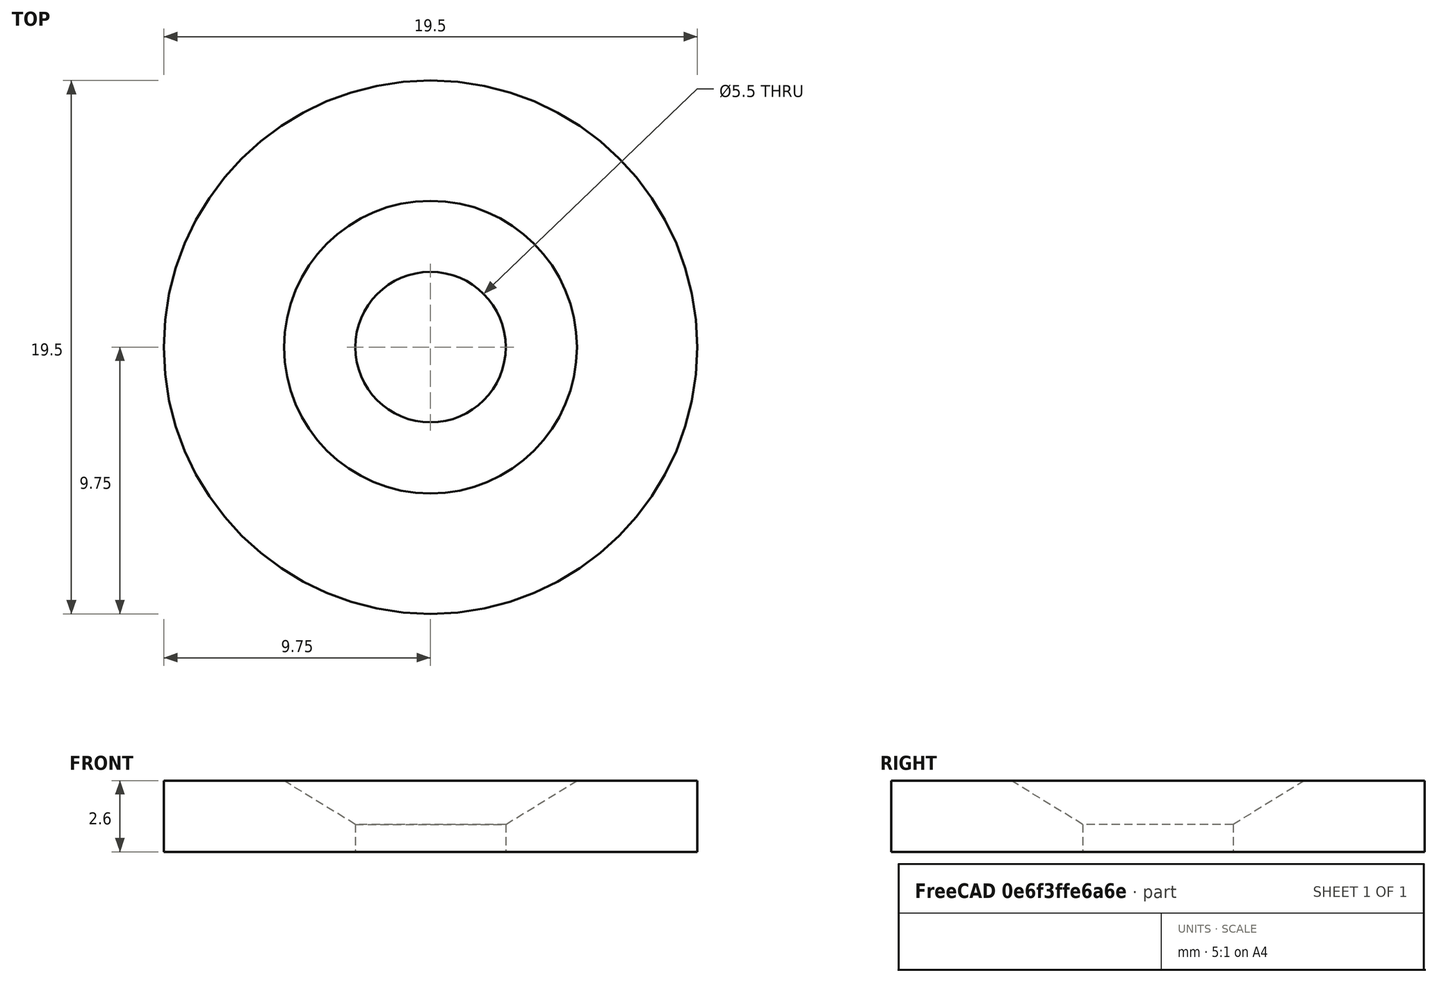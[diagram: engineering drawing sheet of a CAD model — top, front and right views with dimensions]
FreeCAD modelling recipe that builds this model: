
FCSTD DOCUMENT  (FreeCAD 0.22R34137 (Git))
Label: magnet_round_20mm
License: All rights reserved
LicenseURL: http://en.wikipedia.org/wiki/All_rights_reserved
objects: Sketcher::SketchObject×3, PartDesign::Revolution×1, PartDesign::Body×1, Spreadsheet::Sheet×1
note: 6 computed .brp shape members not serialized (recipe doc carries the construction recipe); baked Part::Feature solids carry a one-line shape summary decoded from their .brp

FEATURE [Sketcher::SketchObject] Sketch
  FullyConstrained = true
  MapMode = 5
  Placement = pos=(0,0,0) rot=(0.57735,0.57735,0.57735;2.0944rad)
  Support = -> [YZ_Plane]
  sketch-geometry (5):
    g0: LineSegment StartX=2.75 StartY=0 StartZ=0 EndX=9.75 EndY=0 EndZ=0
    g1: LineSegment StartX=9.75 StartY=0 StartZ=0 EndX=9.75 EndY=2.6 EndZ=0
    g2: LineSegment StartX=9.75 StartY=2.6 StartZ=0 EndX=5.35 EndY=2.6 EndZ=0
    g3: LineSegment StartX=5.35 StartY=2.6 StartZ=0 EndX=2.75 EndY=1 EndZ=0
    g4: LineSegment StartX=2.75 StartY=1 StartZ=0 EndX=2.75 EndY=0 EndZ=0
  constraints (15):
    c: PointOnObject(g0,g-1)
    c: PointOnObject(g0,g-1)
    c: Coincident(g0,g1)
    c: Vertical(g1)
    c: Coincident(g1,g2)
    c: Horizontal(g2)
    c: Coincident(g2,g3)
    c: Coincident(g3,g4)
    c: Coincident(g4,g0)
    c: Vertical(g4)
    c: DistanceX(g0) = 9.75
    c: DistanceX(g0) = 2.75
    c: DistanceY(g1) = 2.6
    c: DistanceX(g2) = 5.35
    c: DistanceY(g4,g4) = 1
FEATURE [PartDesign::Revolution] Revolution
  Angle = 360
  Axis = (-2e-16,3e-16,1)
  Base = (0,0,0)
  Placement = pos=(0,0,0) rot=(0.57735,0.57735,0.57735;2.0944rad)
  Profile = -> Sketch
  ReferenceAxis = -> Sketch [V_Axis]
  Reversed = true
FEATURE [Sketcher::SketchObject] Sketch001  label="inner_circle"
  FullyConstrained = true
  MapMode = 5
  Support = -> [XY_Plane]
  sketch-geometry (1):
    g0: Circle CenterX=0 CenterY=0 CenterZ=0 NormalX=0 NormalY=0 NormalZ=1 AngleXU=0 Radius=2.75
  constraints (2):
    c: Coincident(g0,g-1)
    c: Diameter(g0) = 5.5
FEATURE [Sketcher::SketchObject] Sketch002  label="outer_circle"
  FullyConstrained = true
  MapMode = 5
  Support = -> [XY_Plane]
  sketch-geometry (1):
    g0: Circle CenterX=0 CenterY=0 CenterZ=0 NormalX=0 NormalY=0 NormalZ=1 AngleXU=0 Radius=9.75
  constraints (2):
    c: Coincident(g0,g-1)
    c: Diameter(g0) = 19.5
FEATURE [PartDesign::Body] Body
  Group = -> [Sketch,Revolution,Sketch001,Sketch002]
  Origin = -> Origin
  Tip = -> Revolution
FEATURE [Spreadsheet::Sheet] Spreadsheet  label="Properties"
  cells = C3(outer_d)==19.5 mm; D3(inner_d)==5.5 mm; E3(height)==2.6 mm
